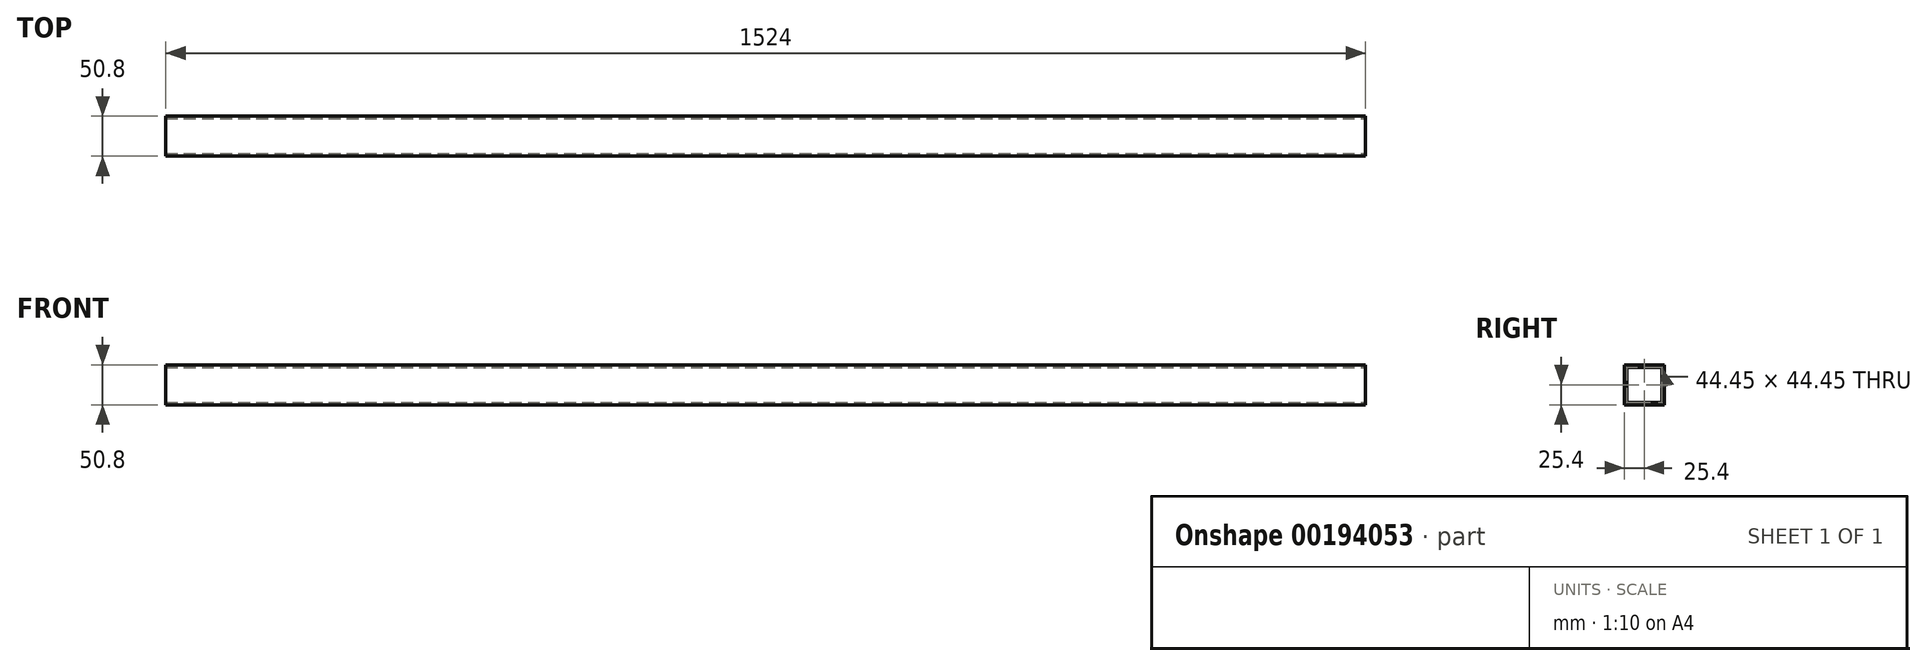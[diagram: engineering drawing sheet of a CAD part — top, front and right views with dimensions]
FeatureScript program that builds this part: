
annotation { "Feature Type Name" : "Feature", "Feature Type Description" : "" }
export const myFeature = defineFeature(function(context is Context, id is Id, definition is map)
    precondition{}
    {
        {
            var Q0;
            Q0=qCreatedBy(makeId("Front.planeOp"),FACE);
            var sketch = newSketch(context, id + "F0", { "sketchPlane" : qUnion([Q0])});
            skLineSegment(sketch, "E0.bottom", {"start": v(-762, -25.4) * mm, "end": v(762, -25.4) * mm});
            skLineSegment(sketch, "E0.top", {"start": v(-762, 25.4) * mm, "end": v(762, 25.4) * mm});
            skLineSegment(sketch, "E0.left", {"start": v(-762, -25.4) * mm, "end": v(-762, 25.4) * mm});
            skLineSegment(sketch, "E0.right", {"start": v(762, -25.4) * mm, "end": v(762, 25.4) * mm});
            skPoint(sketch, "E0.middle", {"position": v(0, 0) * mm});
            skSolve(sketch);
        }
        {
            var Q0;
            Q0=makeQuery(id+"F0.imprint","IMPRINT",FACE,{"disambiguationData":[TD([[makeQuery(id+"F0.imprint","IMPRINT",EDGE,{"derivedFrom":sQuery(id+"F0.wireOp",EDGE,"E0.bottom")}),1.0]])]});
            extrude(context, id + "F1", {"entities" : qUnion([Q0]), "endBound" : BoundingType.SYMMETRIC, "depth" : 50.8 * mm});
        }
        {
            var Q0;
            Q0=makeQuery(id+"F1.opExtrude","SWEPT_FACE",FACE,{"disambiguationData":[OSD([sQuery(id+"F0.wireOp",EDGE,"E0.right")])]});
            var Q1;
            Q1=makeQuery(id+"F1.opExtrude","SWEPT_FACE",FACE,{"disambiguationData":[OSD([sQuery(id+"F0.wireOp",EDGE,"E0.left")])]});
            shell(context, id + "F2", {"entities" : qUnion([Q0, Q1]), "thickness" : 3.17 * mm});
        }
    });
